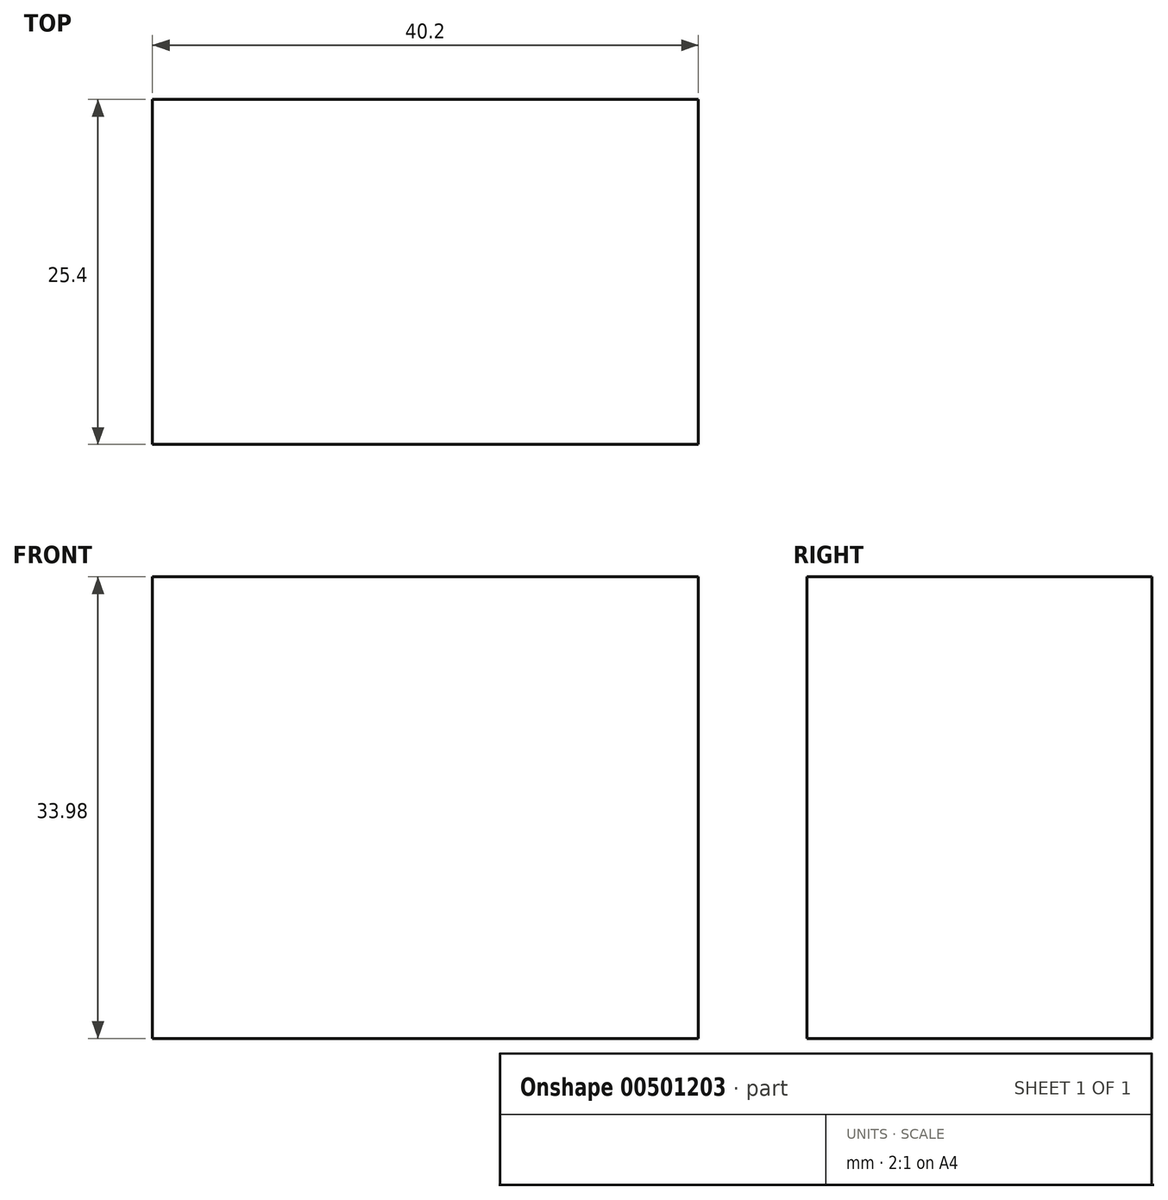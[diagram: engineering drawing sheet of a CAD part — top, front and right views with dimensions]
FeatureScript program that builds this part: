
annotation { "Feature Type Name" : "Feature", "Feature Type Description" : "" }
export const myFeature = defineFeature(function(context is Context, id is Id, definition is map)
    precondition{}
    {
        {
            var Q0;
            Q0=qCreatedBy(makeId("Front.planeOp"),FACE);
            var sketch = newSketch(context, id + "F0", { "sketchPlane" : qUnion([Q0])});
            skLineSegment(sketch, "E0.bottom", {"start": v(-20.1, 17) * mm, "end": v(20.1, 17) * mm});
            skLineSegment(sketch, "E0.top", {"start": v(-20.1, -17) * mm, "end": v(20.1, -17) * mm});
            skLineSegment(sketch, "E0.left", {"start": v(-20.1, 17) * mm, "end": v(-20.1, -17) * mm});
            skLineSegment(sketch, "E0.right", {"start": v(20.1, 17) * mm, "end": v(20.1, -17) * mm});
            skPoint(sketch, "E0.middle", {"position": v(0, 0) * mm});
            skSolve(sketch);
        }
        {
            var Q0;
            Q0=makeQuery(id+"F0.imprint","IMPRINT",FACE,{"disambiguationData":[TD([[makeQuery(id+"F0.imprint","IMPRINT",EDGE,{"derivedFrom":sQuery(id+"F0.wireOp",EDGE,"E0.bottom")}),-1.0]])]});
            extrude(context, id + "F1", {"entities" : qUnion([Q0]), "depth" : 25.4 * mm});
        }
    });
